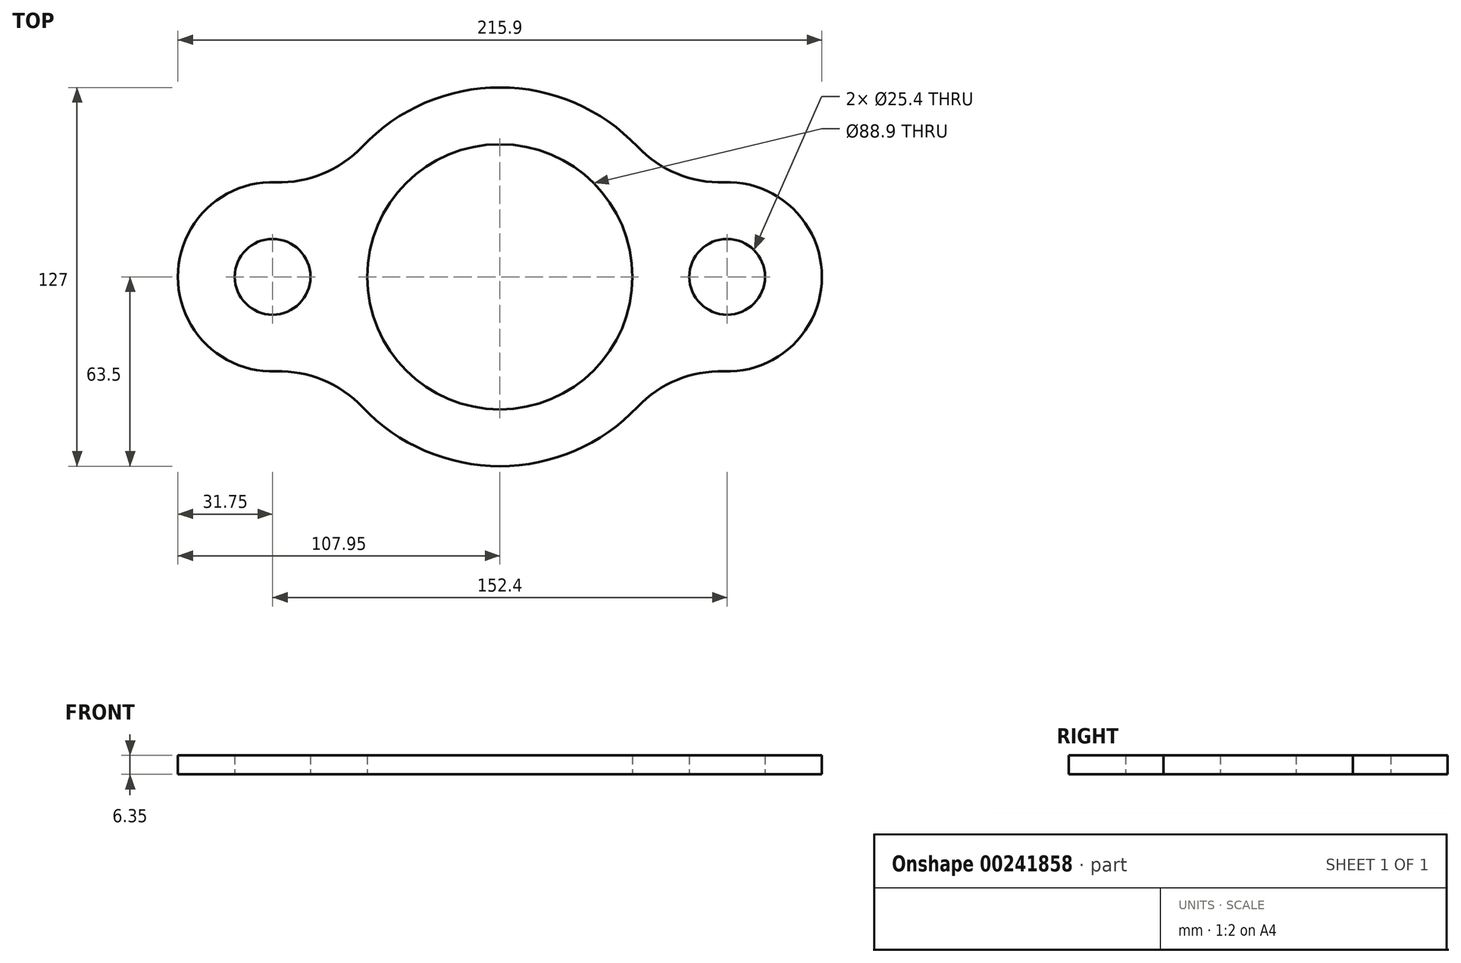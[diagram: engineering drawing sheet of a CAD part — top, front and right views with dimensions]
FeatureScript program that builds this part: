
annotation { "Feature Type Name" : "Feature", "Feature Type Description" : "" }
export const myFeature = defineFeature(function(context is Context, id is Id, definition is map)
    precondition{}
    {
        {
            var Q0;
            Q0=qCreatedBy(makeId("Top.planeOp"),FACE);
            var sketch = newSketch(context, id + "F0", { "sketchPlane" : qUnion([Q0])});
            skCircle(sketch, "E0", {"center": v(0, 0) * mm, "radius": 44.45 * mm});
            skCircle(sketch, "E1", {"center": v(-76.2, 0) * mm, "radius": 12.7 * mm});
            skCircle(sketch, "E2", {"center": v(76.2, 0) * mm, "radius": 12.7 * mm});
            skArc(sketch, "E3", {"start": v(-75.12, 31.73) * mm, "mid": v(-107.95, 0) * mm, "end": v(-75.12, -31.73) * mm});
            skArc(sketch, "E4", {"start": v(75.12, -31.73) * mm, "mid": v(107.95, 0) * mm, "end": v(75.12, 31.73) * mm});
            skArc(sketch, "E5", {"start": v(-46.14, -43.63) * mm, "mid": v(0, -63.5) * mm, "end": v(46.14, -43.63) * mm});
            skArc(sketch, "E6.trimOffspring", {"start": v(46.14, 43.63) * mm, "mid": v(0, 63.5) * mm, "end": v(-46.14, 43.63) * mm});
            skPoint(sketch, "E7.visualSharp", {"position": v(-57.94, 25.98) * mm});
            skArc(sketch, "E7.filletArc", {"start": v(-75.12, 31.73) * mm, "mid": v(-59.35, 34.56) * mm, "end": v(-46.14, 43.63) * mm});
            skPoint(sketch, "E8.visualSharp", {"position": v(57.94, 25.98) * mm});
            skArc(sketch, "E8.filletArc", {"start": v(46.14, 43.63) * mm, "mid": v(59.35, 34.56) * mm, "end": v(75.12, 31.73) * mm});
            skPoint(sketch, "E9.visualSharp", {"position": v(-57.94, -25.98) * mm});
            skArc(sketch, "E9.filletArc", {"start": v(-46.14, -43.63) * mm, "mid": v(-59.35, -34.56) * mm, "end": v(-75.12, -31.73) * mm});
            skPoint(sketch, "E10.visualSharp", {"position": v(57.94, -25.98) * mm});
            skArc(sketch, "E10.filletArc", {"start": v(75.12, -31.73) * mm, "mid": v(59.35, -34.56) * mm, "end": v(46.14, -43.63) * mm});
            skLineSegment(sketch, "E11", {"start": v(-76.2, 0) * mm, "end": v(0, 0) * mm, "construction": true});
            skLineSegment(sketch, "E12", {"start": v(0, 0) * mm, "end": v(76.2, 0) * mm, "construction": true});
            skSolve(sketch);
        }
        {
            var Q0;
            Q0=makeQuery(id+"F0.imprint","IMPRINT",FACE,{"disambiguationData":[TD([[makeQuery(id+"F0.imprint","IMPRINT",EDGE,{"derivedFrom":sQuery(id+"F0.wireOp",EDGE,"E0")}),-1.0]])]});
            var Q1;
            Q1 = qSketchRegion(id + "FSf7PnKduVSaEkD_1", true);
            extrude(context, id + "F1", {"entities" : qUnion([Q0, Q1]), "depth" : 6.35 * mm});
        }
    });
